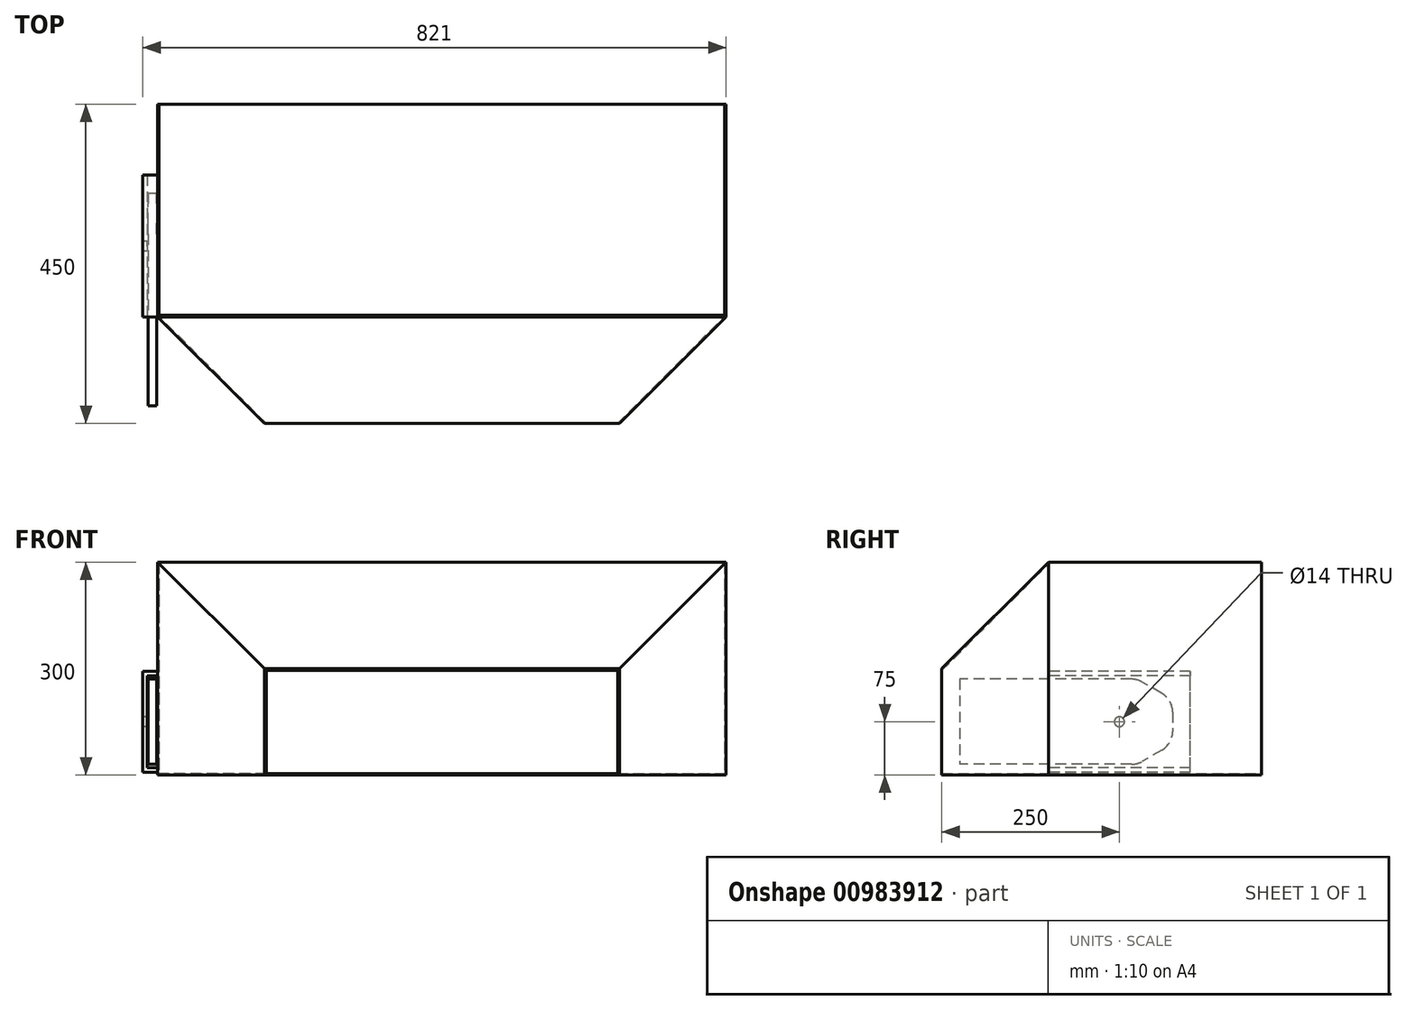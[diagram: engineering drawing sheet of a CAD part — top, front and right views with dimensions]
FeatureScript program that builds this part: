
annotation { "Feature Type Name" : "Feature", "Feature Type Description" : "" }
export const myFeature = defineFeature(function(context is Context, id is Id, definition is map)
    precondition{}
    {
        {
            var Q0;
            Q0=qCreatedBy(makeId("Top.planeOp"),FACE);
            var sketch = newSketch(context, id + "F0", { "sketchPlane" : qUnion([Q0])});
            skLineSegment(sketch, "E0", {"start": v(-250, 0) * mm, "end": v(250, 0) * mm});
            skLineSegment(sketch, "E1", {"start": v(250, 0) * mm, "end": v(400, 150) * mm});
            skLineSegment(sketch, "E2", {"start": v(400, 150) * mm, "end": v(400, 450) * mm});
            skLineSegment(sketch, "E3", {"start": v(-250, 0) * mm, "end": v(-400, 150) * mm});
            skLineSegment(sketch, "E4", {"start": v(-400, 150) * mm, "end": v(-400, 450) * mm});
            skLineSegment(sketch, "E5", {"start": v(-400, 450) * mm, "end": v(400, 450) * mm});
            skSolve(sketch);
        }
        {
            var Q0;
            Q0 = qSketchRegion(id + "F0", true);
            extrude(context, id + "F1", {"entities" : qUnion([Q0]), "depth" : 300 * mm, "offsetDistance" : 25 * mm});
        }
        {
            var Q0;
            Q0=qCreatedBy(makeId("Right.planeOp"),FACE);
            var sketch = newSketch(context, id + "F2", { "sketchPlane" : qUnion([Q0])});
            skLineSegment(sketch, "E6", {"start": v(150, 300) * mm, "end": v(0, 150) * mm});
            skLineSegment(sketch, "E7", {"start": v(0, 150) * mm, "end": v(150, 300) * mm});
            skLineSegment(sketch, "E8", {"start": v(150, 300) * mm, "end": v(0, 300) * mm});
            skLineSegment(sketch, "E9", {"start": v(0, 300) * mm, "end": v(0, 150) * mm});
            skSolve(sketch);
        }
        {
            var Q0;
            Q0 = qSketchRegion(id + "F2", true);
            extrude(context, id + "F3", {"entities" : qUnion([Q0]), "operationType" : NewBodyOperationType.REMOVE, "endBound" : BoundingType.THROUGH_ALL, "oppositeDirection" : true, "depth" : 25 * mm, "offsetDistance" : 25 * mm, "hasSecondDirection" : true, "secondDirectionBound" : SecondDirectionBoundingType.THROUGH_ALL, "secondDirectionOppositeDirection" : false, "secondDirectionDepth" : 25 * mm});
        }
        {
            var Q0;
            Q0=makeQuery(id+"F1.opExtrude","SWEPT_FACE",FACE,{"disambiguationData":[OSD([sQuery(id+"F0.wireOp",EDGE,"E5")])]});
            var Q1;
            Q1=makeQuery(id+"F1.opExtrude","CAP_FACE",FACE,{"disambiguationData":[OSD([sQuery(id+"F0.wireOp",EDGE,"E0"),sQuery(id+"F0.wireOp",EDGE,"E1"),sQuery(id+"F0.wireOp",EDGE,"E2"),sQuery(id+"F0.wireOp",EDGE,"E3"),sQuery(id+"F0.wireOp",EDGE,"E4"),sQuery(id+"F0.wireOp",EDGE,"E5")])],"isStart":false});
            var Q2;
            Q2=makeQuery(id+"F3.boolean.opBoolean","COPY",FACE,{"derivedFrom":makeQuery(id+"F3.opExtrude","SWEPT_FACE",FACE,{"disambiguationData":[OSD([sQuery(id+"F2.wireOp",EDGE,"E7")])]})});
            var Q3;
            Q3=makeQuery(id+"F1.opExtrude","SWEPT_FACE",FACE,{"disambiguationData":[OSD([sQuery(id+"F0.wireOp",EDGE,"E0")])]});
            shell(context, id + "F4", {"entities" : qUnion([Q0, Q1, Q2, Q3]), "thickness" : 2 * mm});
        }
        {
            var Q0;
            Q0=qCreatedBy(makeId("Front.planeOp"),FACE);
            var Q1;
            Q1=makeQuery(id+"F1.opExtrude","CAP_VERTEX",VERTEX,{"disambiguationData":[OSD([sQuery(id+"F0.wireOp",EDGE,"E3"),sQuery(id+"F0.wireOp",EDGE,"E4")])],"isStart":true});
            cPlane(context, id + "F5", {"entities" : qUnion([Q0, Q1]), "cplaneType" : CPlaneType.PLANE_POINT, "offset" : 25 * mm, "width" : 150 * mm, "height" : 150 * mm});
        }
        {
            var Q0;
            Q0=qCreatedBy(id+"F5.planeOp",FACE);
            var sketch = newSketch(context, id + "F6", { "sketchPlane" : qUnion([Q0])});
            skLineSegment(sketch, "E10", {"start": v(-400, 10) * mm, "end": v(-415, 10) * mm});
            skLineSegment(sketch, "E11", {"start": v(-415, 10) * mm, "end": v(-415, 140) * mm});
            skLineSegment(sketch, "E12", {"start": v(-415, 140) * mm, "end": v(-400, 140) * mm});
            skLineSegment(sketch, "E13.0", {"start": v(-421, 146) * mm, "end": v(-400, 146) * mm});
            skLineSegment(sketch, "E13.1", {"start": v(-421, 4) * mm, "end": v(-421, 146) * mm});
            skLineSegment(sketch, "E13.2", {"start": v(-400, 4) * mm, "end": v(-421, 4) * mm});
            skLineSegment(sketch, "E14", {"start": v(-400, 146) * mm, "end": v(-400, 140) * mm});
            skLineSegment(sketch, "E15", {"start": v(-400, 4) * mm, "end": v(-400, 10) * mm});
            skSolve(sketch);
        }
        {
            var Q0;
            Q0 = qSketchRegion(id + "F6", true);
            extrude(context, id + "F7", {"entities" : qUnion([Q0]), "operationType" : NewBodyOperationType.ADD, "oppositeDirection" : true, "depth" : 200 * mm, "offsetDistance" : 25 * mm});
        }
        {
            var Q0;
            Q0=makeQuery(id+"F7.opExtrude","SWEPT_FACE",FACE,{"disambiguationData":[OSD([sQuery(id+"F6.wireOp",EDGE,"E13.1")])]});
            var sketch = newSketch(context, id + "F8", { "sketchPlane" : qUnion([Q0])});
            skCircle(sketch, "E16", {"center": v(-250, 75) * mm, "radius": 7 * mm});
            skLineSegment(sketch, "E17", {"start": v(-350, 75) * mm, "end": v(-150, 75) * mm, "construction": true});
            skSolve(sketch);
        }
        {
            var Q0;
            Q0 = qSketchRegion(id + "F8", true);
            extrude(context, id + "F9", {"entities" : qUnion([Q0]), "operationType" : NewBodyOperationType.REMOVE, "endBound" : BoundingType.UP_TO_NEXT, "oppositeDirection" : true, "depth" : 25 * mm, "offsetDistance" : 25 * mm});
        }
        {
            var Q0;
            Q0=makeQuery(id+"F7.opExtrude","SWEPT_FACE",FACE,{"disambiguationData":[OSD([sQuery(id+"F6.wireOp",EDGE,"E11")])]});
            var Q1;
            Q1=makeQuery(id+"F1.opExtrude","SWEPT_FACE",FACE,{"disambiguationData":[OSD([sQuery(id+"F0.wireOp",EDGE,"E4")])]});
            cPlane(context, id + "F10", {"entities" : qUnion([Q0, Q1]), "cplaneType" : CPlaneType.MID_PLANE, "offset" : 25 * mm, "width" : 150 * mm, "height" : 150 * mm});
        }
        {
            var Q0;
            Q0=qCreatedBy(id+"F10.planeOp",FACE);
            var sketch = newSketch(context, id + "F11", { "sketchPlane" : qUnion([Q0])});
            skLineSegment(sketch, "E18", {"start": v(325, 135) * mm, "end": v(25, 135) * mm});
            skLineSegment(sketch, "E19", {"start": v(325, 135) * mm, "end": v(325, 15) * mm});
            skLineSegment(sketch, "E20", {"start": v(325, 15) * mm, "end": v(25, 15) * mm});
            skLineSegment(sketch, "E21", {"start": v(25, 135) * mm, "end": v(25, 15) * mm});
            skSolve(sketch);
        }
        {
            var Q0;
            Q0 = qSketchRegion(id + "F11", true);
            extrude(context, id + "F12", {"entities" : qUnion([Q0]), "endBound" : BoundingType.SYMMETRIC, "depth" : 12 * mm, "offsetDistance" : 25 * mm});
        }
        {
            var Q0;
            Q0=makeQuery(id+"F12.opExtrude","SWEPT_EDGE",EDGE,{"disambiguationData":[OSD([sQuery(id+"F11.wireOp",EDGE,"E19"),sQuery(id+"F11.wireOp",EDGE,"E20")])]});
            var Q1;
            Q1=makeQuery(id+"F12.opExtrude","SWEPT_EDGE",EDGE,{"disambiguationData":[OSD([sQuery(id+"F11.wireOp",EDGE,"E18"),sQuery(id+"F11.wireOp",EDGE,"E19")])]});
            chamfer(context, id + "F13", {"entities" : qUnion([Q0, Q1]), "chamferType" : ChamferType.OFFSET_ANGLE, "width" : 50 * mm, "oppositeDirection" : true, "angle" : 30 * degree, "tangentPropagation" : true});
        }
        {
            var Q0;
            {var subQ0=sQuery(id+"F11.wireOp",EDGE,"E18");Q0=makeQuery(id+"F13.opChamfer","BLEND_EDGE",EDGE,{"blendedFrom":[makeQuery(id+"F12.opExtrude","SWEPT_EDGE",EDGE,{"disambiguationData":[OSD([subQ0,sQuery(id+"F11.wireOp",EDGE,"E19")])]}),makeQuery(id+"F12.opExtrude","SWEPT_FACE",FACE,{"disambiguationData":[OSD([subQ0])]})],"blendedInto":[makeQuery(id+"F12.opExtrude","SWEPT_FACE",FACE,{"disambiguationData":[OSD([subQ0])]})]});}
            var Q1;
            {var subQ0=sQuery(id+"F11.wireOp",EDGE,"E19");Q1=makeQuery(id+"F13.opChamfer","BLEND_EDGE",EDGE,{"blendedFrom":[makeQuery(id+"F12.opExtrude","SWEPT_EDGE",EDGE,{"disambiguationData":[OSD([sQuery(id+"F11.wireOp",EDGE,"E18"),subQ0])]}),makeQuery(id+"F12.opExtrude","SWEPT_FACE",FACE,{"disambiguationData":[OSD([subQ0])]})],"blendedInto":[makeQuery(id+"F12.opExtrude","SWEPT_FACE",FACE,{"disambiguationData":[OSD([subQ0])]})]});}
            var Q2;
            {var subQ0=sQuery(id+"F11.wireOp",EDGE,"E19");Q2=makeQuery(id+"F13.opChamfer","BLEND_EDGE",EDGE,{"blendedFrom":[makeQuery(id+"F12.opExtrude","SWEPT_EDGE",EDGE,{"disambiguationData":[OSD([subQ0,sQuery(id+"F11.wireOp",EDGE,"E20")])]}),makeQuery(id+"F12.opExtrude","SWEPT_FACE",FACE,{"disambiguationData":[OSD([subQ0])]})],"blendedInto":[makeQuery(id+"F12.opExtrude","SWEPT_FACE",FACE,{"disambiguationData":[OSD([subQ0])]})]});}
            var Q3;
            {var subQ0=sQuery(id+"F11.wireOp",EDGE,"E20");Q3=makeQuery(id+"F13.opChamfer","BLEND_EDGE",EDGE,{"blendedFrom":[makeQuery(id+"F12.opExtrude","SWEPT_EDGE",EDGE,{"disambiguationData":[OSD([sQuery(id+"F11.wireOp",EDGE,"E19"),subQ0])]}),makeQuery(id+"F12.opExtrude","SWEPT_FACE",FACE,{"disambiguationData":[OSD([subQ0])]})],"blendedInto":[makeQuery(id+"F12.opExtrude","SWEPT_FACE",FACE,{"disambiguationData":[OSD([subQ0])]})]});}
            fillet(context, id + "F14", {"entities" : qUnion([Q0, Q1, Q2, Q3]), "radius" : 30 * mm, "tangentPropagation" : true, "allowEdgeOverflow" : false});
        }
    });
